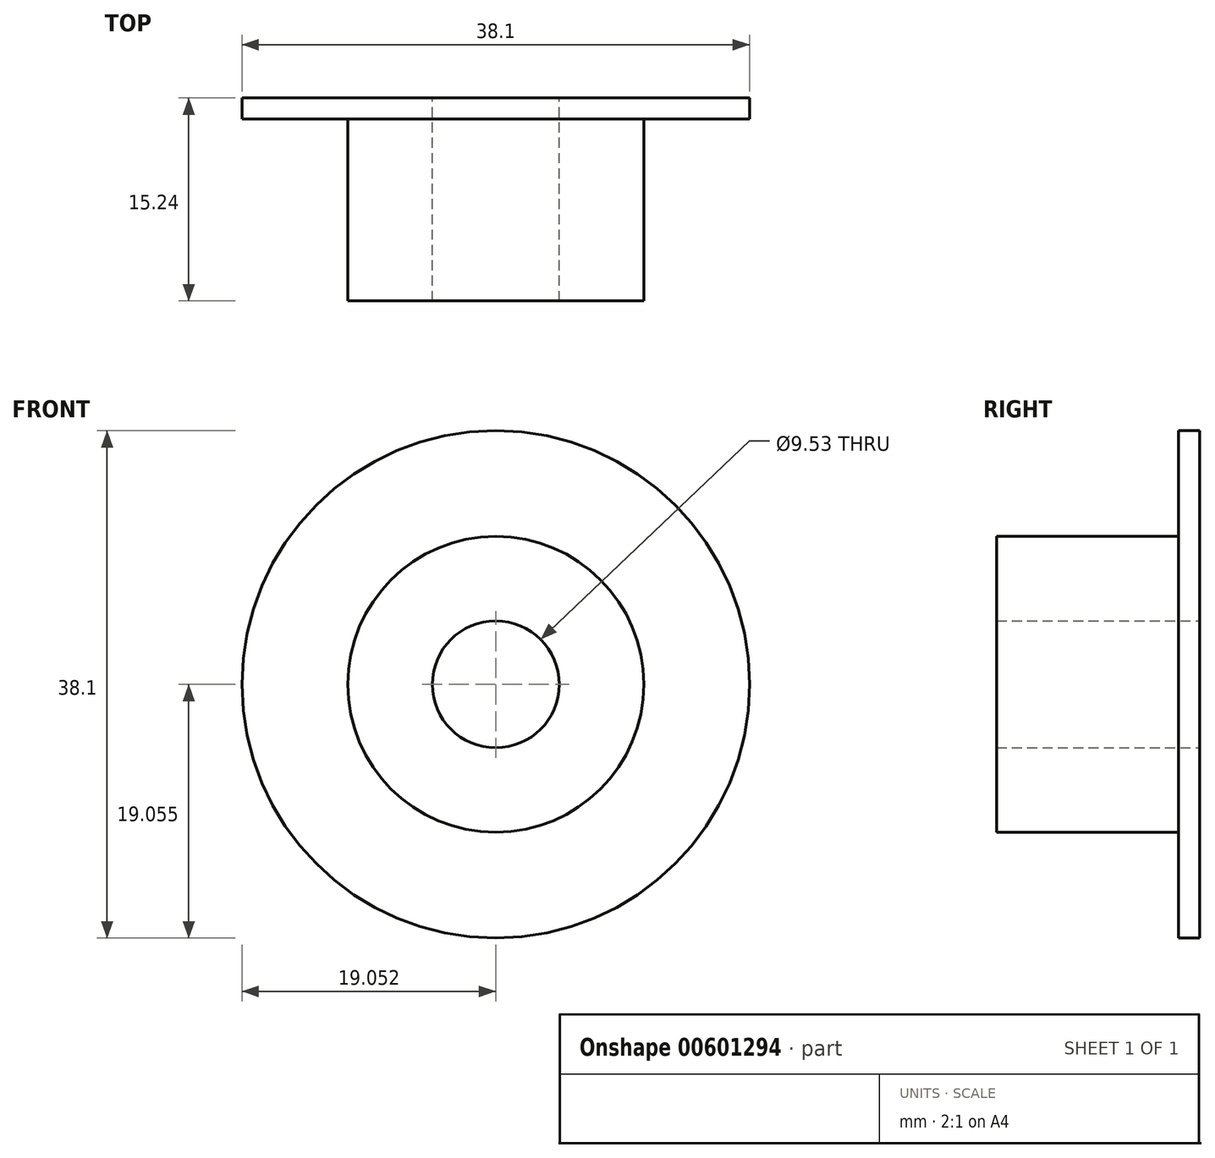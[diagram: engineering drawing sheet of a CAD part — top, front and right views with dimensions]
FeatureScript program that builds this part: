
annotation { "Feature Type Name" : "Feature", "Feature Type Description" : "" }
export const myFeature = defineFeature(function(context is Context, id is Id, definition is map)
    precondition{}
    {
        {
            var Q0;
            Q0=qCreatedBy(makeId("Front.planeOp"),FACE);
            var sketch = newSketch(context, id + "F0", { "sketchPlane" : qUnion([Q0])});
            skCircle(sketch, "E0", {"center": v(-52.2, 27.46) * mm, "radius": 19.05 * mm});
            skCircle(sketch, "E1", {"center": v(-52.2, 27.46) * mm, "radius": 4.76 * mm});
            skSolve(sketch);
        }
        {
            var Q0;
            Q0=makeQuery(id+"F0.imprint","IMPRINT",FACE,{"disambiguationData":[TD([[makeQuery(id+"F0.imprint","IMPRINT",EDGE,{"derivedFrom":sQuery(id+"F0.wireOp",EDGE,"E0")}),1.0]])]});
            extrude(context, id + "F1", {"entities" : qUnion([Q0]), "depth" : 1.59 * mm, "offsetDistance" : 25.4 * mm});
        }
        {
            var Q0;
            Q0=qCreatedBy(makeId("Front.planeOp"),FACE);
            var sketch = newSketch(context, id + "F2", { "sketchPlane" : qUnion([Q0])});
            skCircle(sketch, "E2.0", {"center": v(-52.2, 27.46) * mm, "radius": 4.76 * mm});
            skCircle(sketch, "E3", {"center": v(-52.2, 27.46) * mm, "radius": 11.11 * mm});
            skSolve(sketch);
        }
        {
            var Q0;
            Q0 = qSketchRegion(id + "F2", true);
            var Q1;
            Q1 = qConstructionFilter(qBodyType(qCreatedBy(id + "F2" ,EDGE), BodyType.WIRE), ConstructionObject.NO);
            extrude(context, id + "F3", {"entities" : qUnion([Q0]), "operationType" : NewBodyOperationType.ADD, "surfaceEntities" : qUnion([Q1]), "depth" : 15.24 * mm, "offsetDistance" : 25.4 * mm});
        }
    });
